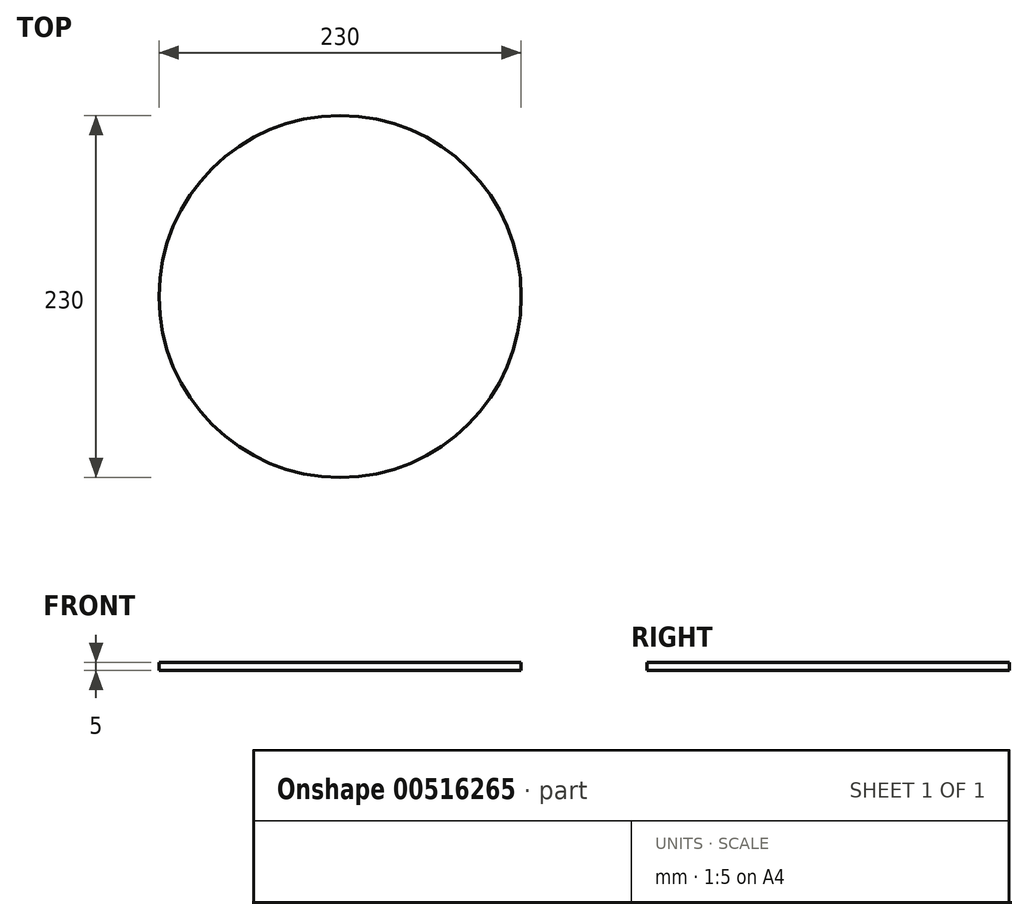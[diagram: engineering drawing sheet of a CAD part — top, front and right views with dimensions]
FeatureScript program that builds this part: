
annotation { "Feature Type Name" : "Feature", "Feature Type Description" : "" }
export const myFeature = defineFeature(function(context is Context, id is Id, definition is map)
    precondition{}
    {
        {
            var Q0;
            Q0=qCreatedBy(makeId("Top.planeOp"),FACE);
            var sketch = newSketch(context, id + "F0", { "sketchPlane" : qUnion([Q0])});
            skCircle(sketch, "E0", {"center": v(0, 0) * mm, "radius": 115 * mm});
            skSolve(sketch);
        }
        {
            var Q0;
            Q0=makeQuery(id+"F0.imprint","IMPRINT",FACE,{"disambiguationData":[TD([[makeQuery(id+"F0.imprint","IMPRINT",EDGE,{"derivedFrom":sQuery(id+"F0.wireOp",EDGE,"E0")}),1.0]])]});
            extrude(context, id + "F1", {"entities" : qUnion([Q0]), "depth" : 5 * mm, "offsetDistance" : 25 * mm});
        }
    });
